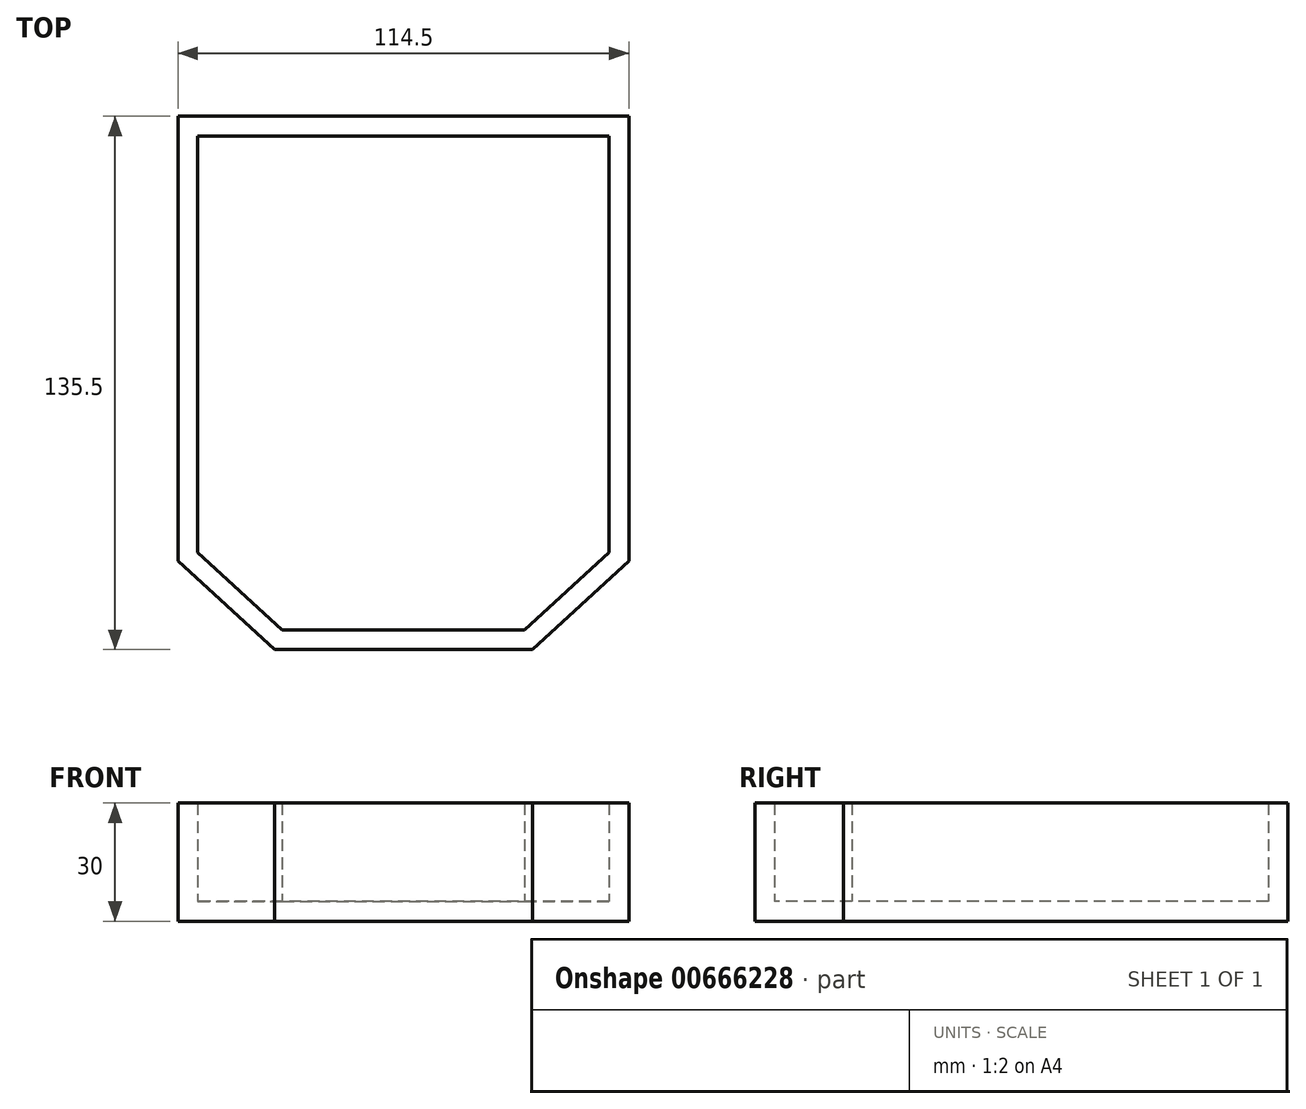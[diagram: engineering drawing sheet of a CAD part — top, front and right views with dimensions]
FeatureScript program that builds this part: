
annotation { "Feature Type Name" : "Feature", "Feature Type Description" : "" }
export const myFeature = defineFeature(function(context is Context, id is Id, definition is map)
    precondition{}
    {
        {
            var Q0;
            Q0=qCreatedBy(makeId("Top.planeOp"),FACE);
            var sketch = newSketch(context, id + "F0", { "sketchPlane" : qUnion([Q0])});
            skLineSegment(sketch, "E0.bottom", {"start": v(-58.1, 42.38) * mm, "end": v(56.4, 42.38) * mm});
            skLineSegment(sketch, "E0.top", {"start": v(-33.6, -93.12) * mm, "end": v(31.9, -93.12) * mm});
            skLineSegment(sketch, "E0.left", {"start": v(-58.1, 42.38) * mm, "end": v(-58.1, -70.62) * mm});
            skLineSegment(sketch, "E0.right", {"start": v(56.4, 42.38) * mm, "end": v(56.4, -70.62) * mm});
            skLineSegment(sketch, "E1", {"start": v(31.9, -93.12) * mm, "end": v(56.4, -70.62) * mm});
            skLineSegment(sketch, "E2", {"start": v(-33.6, -93.12) * mm, "end": v(-58.1, -70.62) * mm});
            skPoint(sketch, "E3.orphan", {"position": v(-58.1, -93.12) * mm});
            skPoint(sketch, "E4.orphan", {"position": v(56.4, -93.12) * mm});
            skSolve(sketch);
        }
        {
            var Q0;
            Q0 = qSketchRegion(id + "F0", true);
            extrude(context, id + "F1", {"entities" : qUnion([Q0]), "depth" : 5 * mm, "offsetDistance" : 25 * mm});
        }
        {
            var Q0;
            Q0=makeQuery(id+"F1.opExtrude","CAP_FACE",FACE,{"disambiguationData":[OSD([sQuery(id+"F0.wireOp",EDGE,"E0.bottom"),sQuery(id+"F0.wireOp",EDGE,"E0.top"),sQuery(id+"F0.wireOp",EDGE,"E0.left"),sQuery(id+"F0.wireOp",EDGE,"E0.right"),sQuery(id+"F0.wireOp",EDGE,"E1"),sQuery(id+"F0.wireOp",EDGE,"E2")])],"isStart":false});
            var sketch = newSketch(context, id + "F2", { "sketchPlane" : qUnion([Q0])});
            skLineSegment(sketch, "E5.0", {"start": v(-53.1, 37.38) * mm, "end": v(-53.1, -68.42) * mm});
            skLineSegment(sketch, "E5.1", {"start": v(-31.65, -88.12) * mm, "end": v(29.95, -88.12) * mm});
            skLineSegment(sketch, "E5.2", {"start": v(29.95, -88.12) * mm, "end": v(51.4, -68.42) * mm});
            skLineSegment(sketch, "E5.3", {"start": v(-53.1, -68.42) * mm, "end": v(-31.65, -88.12) * mm});
            skLineSegment(sketch, "E5.4", {"start": v(51.4, -68.42) * mm, "end": v(51.4, 37.38) * mm});
            skLineSegment(sketch, "E5.5", {"start": v(51.4, 37.38) * mm, "end": v(-53.1, 37.38) * mm});
            skSolve(sketch);
        }
        {
            var Q0;
            Q0=makeQuery(id+"F2.imprint","IMPRINT",FACE,{"disambiguationData":[TD([[makeQuery(id+"F2.imprint","IMPRINT",EDGE,{"derivedFrom":sQuery(id+"F2.wireOp",EDGE,"E5.0")}),-1.0]])]});
            extrude(context, id + "F3", {"entities" : qUnion([Q0]), "operationType" : NewBodyOperationType.ADD, "depth" : 25 * mm, "offsetDistance" : 25 * mm});
        }
    });
